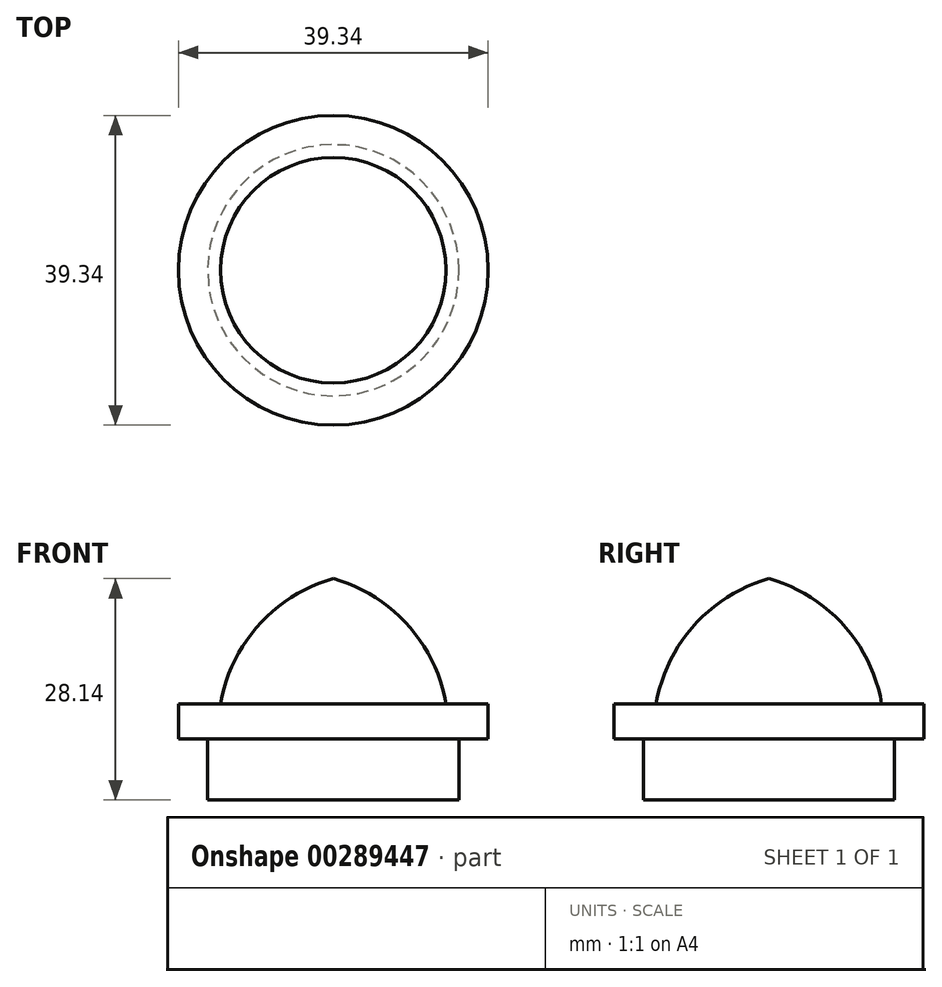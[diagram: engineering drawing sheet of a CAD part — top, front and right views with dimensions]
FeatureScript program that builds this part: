
annotation { "Feature Type Name" : "Feature", "Feature Type Description" : "" }
export const myFeature = defineFeature(function(context is Context, id is Id, definition is map)
    precondition{}
    {
        {
            var Q0;
            Q0=qCreatedBy(makeId("Front.planeOp"),FACE);
            var sketch = newSketch(context, id + "F0", { "sketchPlane" : qUnion([Q0])});
            skLineSegment(sketch, "E0", {"start": v(0, 0) * mm, "end": v(15.96, 0) * mm});
            skLineSegment(sketch, "E1", {"start": v(15.96, 0) * mm, "end": v(15.96, 7.8) * mm});
            skLineSegment(sketch, "E2", {"start": v(15.96, 7.8) * mm, "end": v(19.67, 7.8) * mm});
            skLineSegment(sketch, "E3", {"start": v(19.67, 7.8) * mm, "end": v(19.67, 12.25) * mm});
            skLineSegment(sketch, "E4", {"start": v(19.67, 12.25) * mm, "end": v(0, 12.25) * mm});
            skLineSegment(sketch, "E5", {"start": v(0, 12.25) * mm, "end": v(0, 0) * mm});
            skSolve(sketch);
        }
        {
            var Q0;
            Q0=makeQuery(id+"F0.imprint","IMPRINT",FACE,{"disambiguationData":[TD([[makeQuery(id+"F0.imprint","IMPRINT",EDGE,{"derivedFrom":sQuery(id+"F0.wireOp",EDGE,"E0")}),1.0]])]});
            var Q1;
            Q1=sQuery(id+"F0.wireOp",EDGE,"E5");
            revolve(context, id + "F1", {"entities" : qUnion([Q0]), "axis" : qUnion([Q1]), "revolveType" : RevolveType.FULL});
        }
        {
            var Q0;
            Q0=qCreatedBy(makeId("Front.planeOp"),FACE);
            var sketch = newSketch(context, id + "F2", { "sketchPlane" : qUnion([Q0])});
            skArc(sketch, "E6", {"start": v(14.46, 11.36) * mm, "mid": v(9.75, 21.92) * mm, "end": v(0, 28.14) * mm});
            skLineSegment(sketch, "E7", {"start": v(0, 28.14) * mm, "end": v(0, 11.36) * mm});
            skLineSegment(sketch, "E8", {"start": v(0, 11.36) * mm, "end": v(14.46, 11.36) * mm});
            skSolve(sketch);
        }
        {
            var Q0;
            Q0=makeQuery(id+"F2.imprint","IMPRINT",FACE,{"disambiguationData":[TD([[makeQuery(id+"F2.imprint","IMPRINT",EDGE,{"derivedFrom":sQuery(id+"F2.wireOp",EDGE,"E6")}),1.0]])]});
            var Q1;
            Q1=sQuery(id+"F2.wireOp",EDGE,"E7");
            revolve(context, id + "F3", {"operationType" : NewBodyOperationType.ADD, "entities" : qUnion([Q0]), "axis" : qUnion([Q1]), "revolveType" : RevolveType.FULL});
        }
    });
